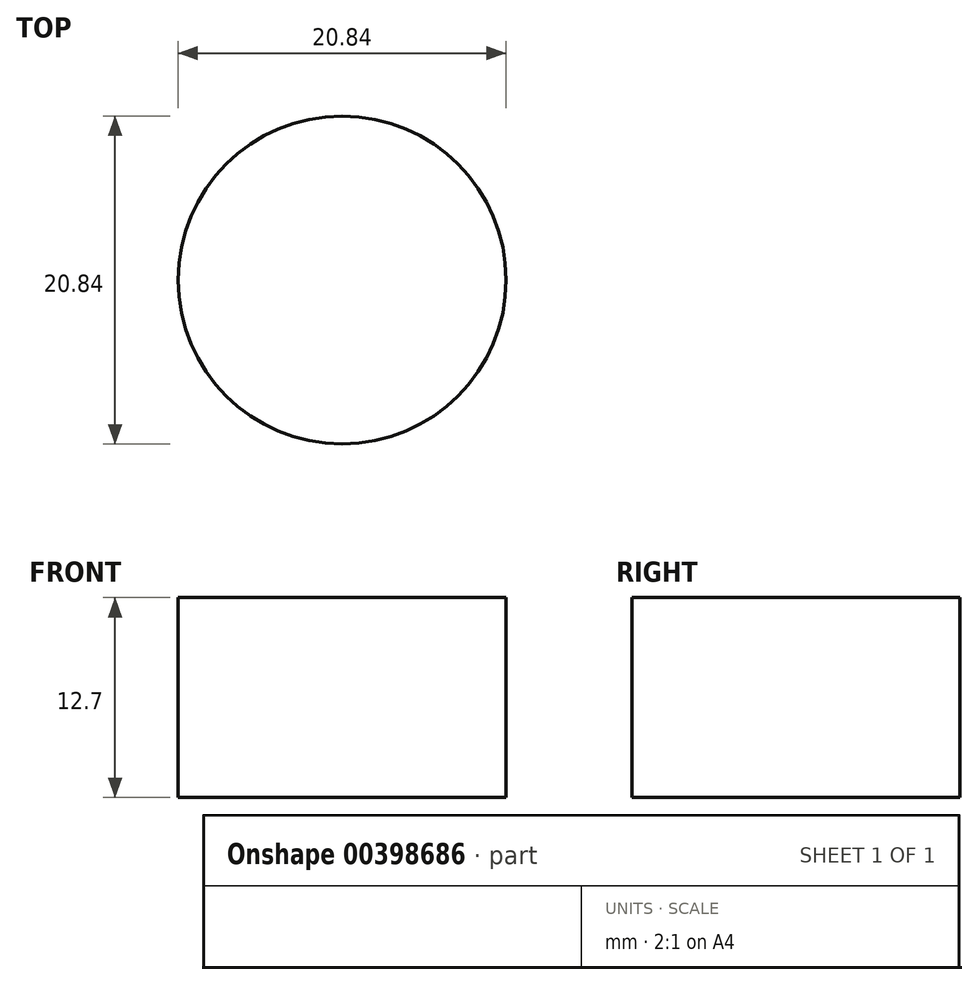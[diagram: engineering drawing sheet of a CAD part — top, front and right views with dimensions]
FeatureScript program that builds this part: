
annotation { "Feature Type Name" : "Feature", "Feature Type Description" : "" }
export const myFeature = defineFeature(function(context is Context, id is Id, definition is map)
    precondition{}
    {
        {
            var Q0;
            Q0=qCreatedBy(makeId("Top.planeOp"),FACE);
            var sketch = newSketch(context, id + "F0", { "sketchPlane" : qUnion([Q0])});
            skCircle(sketch, "E0", {"center": v(0, 0) * mm, "radius": 10.42 * mm});
            skSolve(sketch);
        }
        {
            var Q0;
            Q0=makeQuery(id+"F0.imprint","IMPRINT",FACE,{"disambiguationData":[TD([[makeQuery(id+"F0.imprint","IMPRINT",EDGE,{"derivedFrom":sQuery(id+"F0.wireOp",EDGE,"E0")}),1.0]])]});
            extrude(context, id + "F1", {"entities" : qUnion([Q0]), "depth" : 12.7 * mm});
        }
    });
